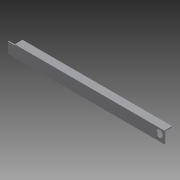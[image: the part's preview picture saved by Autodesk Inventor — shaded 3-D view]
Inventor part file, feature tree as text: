
AUTODESK INVENTOR PART (.ipt)
format: ipt  version: 2012 (Build 160160000, 160)  size: 91,136 bytes
history: native  units: in
note: dims shown in document units (in); Inventor stores cm internally (conversion verified against a paired STEP export)
features: extrude x3, sketch x3
ambient origin geometry x8: Origin, YZ Plane, XZ Plane, XY Plane, X Axis, Y Axis, Z Axis, Center Point
bodies: Solid1 (feature_tree)
feature tree (6):
  extrude  "Extrusion1"  Depth=1.0in
  extrude  "Extrusion2"  Depth=0.125in
  extrude  "Extrusion3"  Depth=20.0in TaperAngle=0.0deg
  sketch  "Sketch1"  dims[d0=1.5in d1=1.0in]
  sketch  "Sketch2"  dims[d2=0.125in d3=0.125in]
  sketch  "Sketch3"  dims[d4=20.0in d5=0.0in d11=20.0in d12=0.0in d13=0.625in d14=0.625in d15=0.875in d16=0.875in d17=0.125in d18=0.0in]
